# Revit family: Legrand_Lighting_Management_Interface_Actuator.
name_source: partatom
category: Dispositifs d'éclairage
units: mm (PartAtom-declared; Revit-internal decimal feet)

## family parameters
Conserver l'orientation des annotations = Non
Cote de connecteur circulaire = Utiliser le diamètre
Couper avec des vides une fois chargée = Non
Hôte = Face
Partagée = Non
Point de calcul de pièce = Non
Type d'élément = Normal

## types (1)
- Radio/KNX
    Alarm function = Non
    Collecteur de terre = Non
    Colour = <Par catégorie>
    Constant light control = Non
    Cosses d'artère secondaire = Non
    Degree of protection (IP) = IP20
    Description = KNX/RADIO INTERFACE
    Detection angle horizontal (MAX) (°) = 0
    Detection angle horizontal (MIN) (°) = 0
    Diameter detection range on floor (m) = 0
    Dim function with dimmer basic element = Non
    Elévation par défaut = 1219 mm
    Fabricant = Legrand
    Forced switch off = Non
    Frequency (MAX) (Hz) = 0
    Frequency (MIN) (Hz) = 0
    General Conditions of Use = https://export.legrand.com
    HVAC-control = Non
    Liaison neutre = Non
    Max. duty cycle (mn) = 0
    Max. starting current (A) = 0
    Max. switching power (W) = 0
    Max. transmission range frontally (m) = 0
    Max. transmission range sideways (m) = 0
    Maximum mounting height (m) = 0
    Min. switch-on time (s) = 0
    Modèle = 048877
    Mounting method = Surface mounted (plaster)
    Nominal voltage (V) = 0
    RAL-number (akin) = 0
    Remote operation = Non
    Response value luminosity (MAX) (lx) = 0
    Response value luminosity (MIN) (lx) = 0
    Response value luminosity adjustable = Non
    Response value sensitivity adjustable = Non
    Substation input = Non
    Suitable for wireless transmission = Non
    Temperature (MAX) (°C) = 0
    Temperature (MIN) (°C) = 0
    URL = http://www.legrandoc.com
